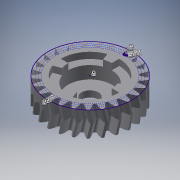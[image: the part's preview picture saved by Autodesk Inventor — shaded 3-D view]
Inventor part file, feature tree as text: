
AUTODESK INVENTOR PART (.ipt)
format: ipt  version: 2017 (Build 210142000, 142)  size: 1,004,032 bytes
history: native  units: mm
features: sketch x5, extrude x5, pattern_circular x3, helix x2, projected_geometry x1
ambient origin geometry x8: Origin, YZ Plane, XZ Plane, XY Plane, X Axis, Y Axis, Z Axis, Center Point
bodies: Solid1 (feature_tree)
feature tree (16):
  sketch  "Sketch1"  dims[d0=20.0mm d1=0.0mm]
  extrude  "Extrusion1"  TaperAngle=0.0deg  [1 undecoded]
  extrude  "Extrusion2"  Depth=250.0mm TaperAngle=360.0deg
  pattern_circular  "Circular Pattern1"  [2 undecoded]
  extrude  "Extrusion3"  Depth=6.0mm
  extrude  "Extrusion4"  Depth=12.217305mm
  extrude  "Extrusion5"  Depth=5.0mm TaperAngle=0.0deg
  pattern_circular  "Circular Pattern2"  Count=4 Angle=360.0deg
  helix  "Coil1"  [1 undecoded]
  helix  "Coil2"  [1 undecoded]
  pattern_circular  "Circular Pattern3"  [2 undecoded]
  sketch  "Sketch2"  dims[d2=10.0mm d3=0.0mm d4=250.0mm d5=360.0deg]
  sketch  "Sketch3"  dims[d7=13.5mm]
  sketch  "Sketch4"  dims[d8=10.0mm d9=0.0mm]
  sketch  "Sketch5"  dims[d10=35.0mm d11=15.0mm d12=0.0mm d13=6.0mm d14=12.217305mm d15=5.0mm d16=0.0mm d17=40.0mm d18=360.0deg d20=10.0mm d21=10.0mm d22=0.1mm d23=0.0mm d24=90.0deg d25=90.0deg d26=0.0mm d27=0.0mm d28=10.0mm d29=10.0mm d30=0.1mm d31=0.0mm d32=90.0deg d33=90.0deg d34=0.0mm d35=0.0mm d36=250.0mm d37=360.0deg]
  projected_geometry  "Projected Loop1"
note: 7 required parameter values undecoded (feature->parameter linkage not recoverable at this tier; creation-order binding heuristic only, values carry confidence <= 0.55)
